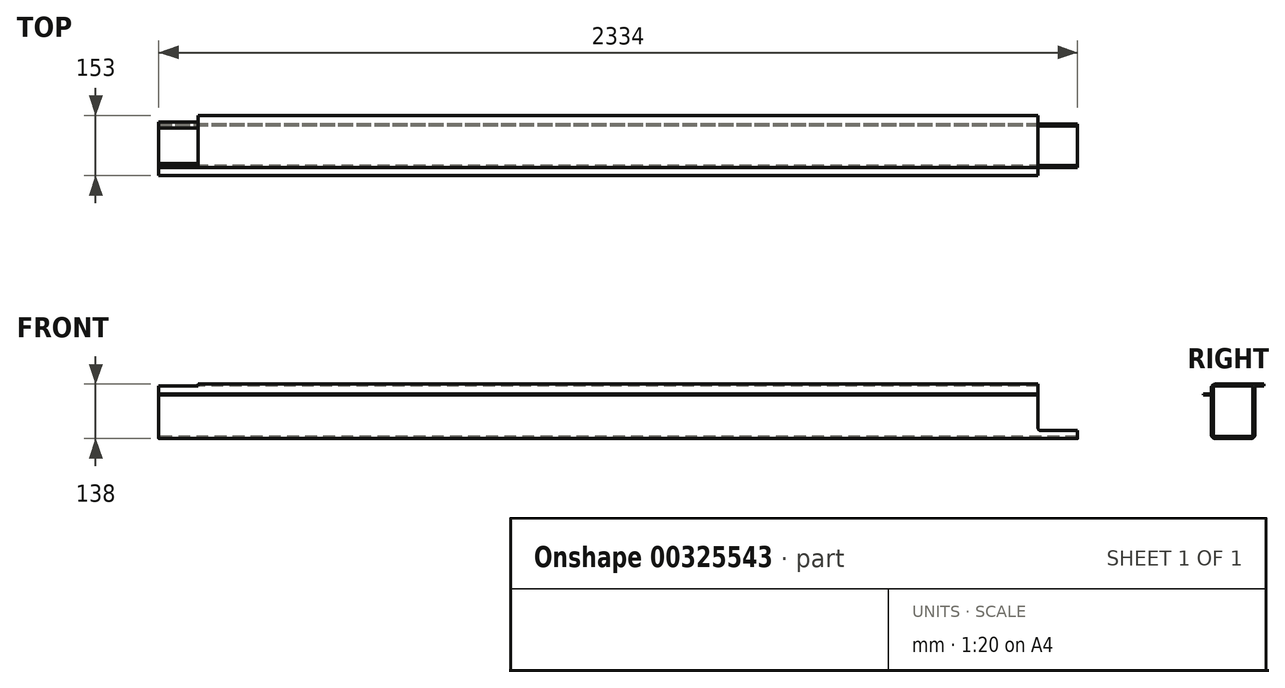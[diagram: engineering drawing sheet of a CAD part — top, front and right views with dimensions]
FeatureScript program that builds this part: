
annotation { "Feature Type Name" : "Feature", "Feature Type Description" : "" }
export const myFeature = defineFeature(function(context is Context, id is Id, definition is map)
    precondition{}
    {
        {
            var Q0;
            Q0=qCreatedBy(makeId("Right.planeOp"),FACE);
            var sketch = newSketch(context, id + "F0", { "sketchPlane" : qUnion([Q0])});
            skLineSegment(sketch, "E0", {"start": v(127.57, 22.43) * mm, "end": v(4.57, 22.43) * mm});
            skLineSegment(sketch, "E1", {"start": v(-5.43, 12.43) * mm, "end": v(-5.43, -0.57) * mm});
            skLineSegment(sketch, "E2", {"start": v(-7.43, -2.57) * mm, "end": v(-25.43, -2.57) * mm});
            skLineSegment(sketch, "E3", {"start": v(-25.43, -2.57) * mm, "end": v(-25.43, -4.57) * mm});
            skLineSegment(sketch, "E4", {"start": v(-25.43, -4.57) * mm, "end": v(-7.43, -4.57) * mm});
            skLineSegment(sketch, "E5", {"start": v(-5.43, -6.57) * mm, "end": v(-5.43, -105.57) * mm});
            skLineSegment(sketch, "E6", {"start": v(4.57, -115.57) * mm, "end": v(95.57, -115.57) * mm});
            skLineSegment(sketch, "E7", {"start": v(105.57, -105.57) * mm, "end": v(105.57, 12.43) * mm});
            skLineSegment(sketch, "E8", {"start": v(110.57, 17.43) * mm, "end": v(127.57, 17.43) * mm});
            skLineSegment(sketch, "E9", {"start": v(127.57, 17.43) * mm, "end": v(127.57, 22.43) * mm});
            skLineSegment(sketch, "E10.0", {"start": v(100.57, -105.57) * mm, "end": v(100.57, 12.43) * mm});
            skLineSegment(sketch, "E11.0", {"start": v(4.6, -110.57) * mm, "end": v(95.57, -110.57) * mm});
            skLineSegment(sketch, "E12", {"start": v(95.57, 17.43) * mm, "end": v(4.98, 17.43) * mm});
            skLineSegment(sketch, "E13", {"start": v(-0.4, -105.55) * mm, "end": v(-0.02, 12.45) * mm});
            skPoint(sketch, "E14.visualSharp", {"position": v(0, 17.43) * mm});
            skArc(sketch, "E14.filletArc", {"start": v(4.98, 17.43) * mm, "mid": v(1.45, 15.97) * mm, "end": v(-0.02, 12.45) * mm});
            skPoint(sketch, "E15.visualSharp", {"position": v(100.57, 17.43) * mm});
            skArc(sketch, "E15.filletArc", {"start": v(100.57, 12.43) * mm, "mid": v(99.1, 15.96) * mm, "end": v(95.57, 17.43) * mm});
            skPoint(sketch, "E16.visualSharp", {"position": v(100.57, -110.57) * mm});
            skArc(sketch, "E16.filletArc", {"start": v(95.57, -110.57) * mm, "mid": v(99.1, -109.1) * mm, "end": v(100.57, -105.57) * mm});
            skPoint(sketch, "E17.visualSharp", {"position": v(-0.43, -110.57) * mm});
            skArc(sketch, "E17.filletArc", {"start": v(-0.4, -105.55) * mm, "mid": v(1.05, -109.1) * mm, "end": v(4.6, -110.57) * mm});
            skPoint(sketch, "E18.visualSharp", {"position": v(105.57, 17.43) * mm});
            skArc(sketch, "E18.filletArc", {"start": v(110.57, 17.43) * mm, "mid": v(107.04, 15.96) * mm, "end": v(105.57, 12.43) * mm});
            skPoint(sketch, "E19.visualSharp", {"position": v(-5.43, -2.57) * mm});
            skArc(sketch, "E19.filletArc", {"start": v(-7.43, -2.57) * mm, "mid": v(-6.01, -1.99) * mm, "end": v(-5.43, -0.57) * mm});
            skPoint(sketch, "E20.visualSharp", {"position": v(-5.43, -4.57) * mm});
            skArc(sketch, "E20.filletArc", {"start": v(-5.43, -6.57) * mm, "mid": v(-6.01, -5.16) * mm, "end": v(-7.43, -4.57) * mm});
            skPoint(sketch, "E21.visualSharp", {"position": v(-5.43, 22.43) * mm});
            skArc(sketch, "E21.filletArc", {"start": v(4.57, 22.43) * mm, "mid": v(-2.5, 19.5) * mm, "end": v(-5.43, 12.43) * mm});
            skPoint(sketch, "E22.visualSharp", {"position": v(-5.43, -115.57) * mm});
            skArc(sketch, "E22.filletArc", {"start": v(-5.43, -105.57) * mm, "mid": v(-2.5, -112.64) * mm, "end": v(4.57, -115.57) * mm});
            skPoint(sketch, "E23.visualSharp", {"position": v(105.57, -115.57) * mm});
            skArc(sketch, "E23.filletArc", {"start": v(95.57, -115.57) * mm, "mid": v(102.65, -112.64) * mm, "end": v(105.57, -105.57) * mm});
            skSolve(sketch);
        }
        {
            var Q0;
            Q0=makeQuery(id+"F0.imprint","IMPRINT",FACE,{"disambiguationData":[TD([[makeQuery(id+"F0.imprint","IMPRINT",EDGE,{"derivedFrom":sQuery(id+"F0.wireOp",EDGE,"E0")}),1.0]])]});
            extrude(context, id + "F1", {"entities" : qUnion([Q0]), "depth" : 2334 * mm});
        }
        {
            var Q0;
            Q0=makeQuery(id+"F1.opExtrude","SWEPT_FACE",FACE,{"disambiguationData":[OSD([sQuery(id+"F0.wireOp",EDGE,"E9")])]});
            var sketch = newSketch(context, id + "F2", { "sketchPlane" : qUnion([Q0])});
            skLineSegment(sketch, "E24", {"start": v(-2334, 22.43) * mm, "end": v(-2234, 22.43) * mm});
            skLineSegment(sketch, "E25", {"start": v(-2234, 22.43) * mm, "end": v(-2234, -89.57) * mm});
            skLineSegment(sketch, "E26", {"start": v(-2239, -94.57) * mm, "end": v(-2334, -94.57) * mm});
            skLineSegment(sketch, "E27", {"start": v(-2334, -94.57) * mm, "end": v(-2334, 22.43) * mm});
            skPoint(sketch, "E28.visualSharp", {"position": v(-2234, -94.57) * mm});
            skArc(sketch, "E28.filletArc", {"start": v(-2239, -94.57) * mm, "mid": v(-2235.46, -93.1) * mm, "end": v(-2234, -89.57) * mm});
            skArc(sketch, "E29.MirrorCS", {"start": v(-95, -94.57) * mm, "mid": v(-98.54, -93.1) * mm, "end": v(-100, -89.57) * mm});
            skLineSegment(sketch, "E30.MirrorCS", {"start": v(-100, 22.43) * mm, "end": v(-100, -89.57) * mm});
            skLineSegment(sketch, "E31.MirrorCS", {"start": v(0, 22.43) * mm, "end": v(-100, 22.43) * mm});
            skPoint(sketch, "E32.MirrorP", {"position": v(-100, -94.57) * mm});
            skLineSegment(sketch, "E33.MirrorCS", {"start": v(0, -94.57) * mm, "end": v(0, 22.43) * mm});
            skLineSegment(sketch, "E34.MirrorCS", {"start": v(-95, -94.57) * mm, "end": v(0, -94.57) * mm});
            skSolve(sketch);
        }
        {
            var Q0;
            {var subQ5=sQuery(id+"F2.wireOp",EDGE,"E29.MirrorCS");Q0=makeQuery(id+"F2.imprint","IMPRINT",FACE,{"disambiguationData":[TD([[makeQuery(id+"F2.imprint","IMPRINT",EDGE,{"derivedFrom":subQ5}),-1.0]])]});}
            var Q1;
            {var subQ4=sQuery(id+"F2.wireOp",EDGE,"E26");Q1=makeQuery(id+"F2.imprint","IMPRINT",FACE,{"disambiguationData":[TD([[makeQuery(id+"F2.imprint","IMPRINT",EDGE,{"derivedFrom":subQ4}),-1.0]])]});}
            var Q2;
            {var subQ0=sQuery(id+"F2.wireOp",EDGE,"E24");Q2=makeQuery(id+"F2.imprint","IMPRINT",FACE,{"disambiguationData":[TD([[makeQuery(id+"F2.imprint","IMPRINT",EDGE,{"derivedFrom":subQ0}),-1.0]])]});}
            var Q3;
            {var subQ0=sQuery(id+"F2.wireOp",EDGE,"E31.MirrorCS");Q3=makeQuery(id+"F2.imprint","IMPRINT",FACE,{"disambiguationData":[TD([[makeQuery(id+"F2.imprint","IMPRINT",EDGE,{"derivedFrom":subQ0}),-1.0]])]});}
            extrude(context, id + "F3", {"entities" : qUnion([Q0, Q1, Q2, Q3]), "operationType" : NewBodyOperationType.REMOVE, "oppositeDirection" : true, "depth" : 155 * mm});
        }
    });
